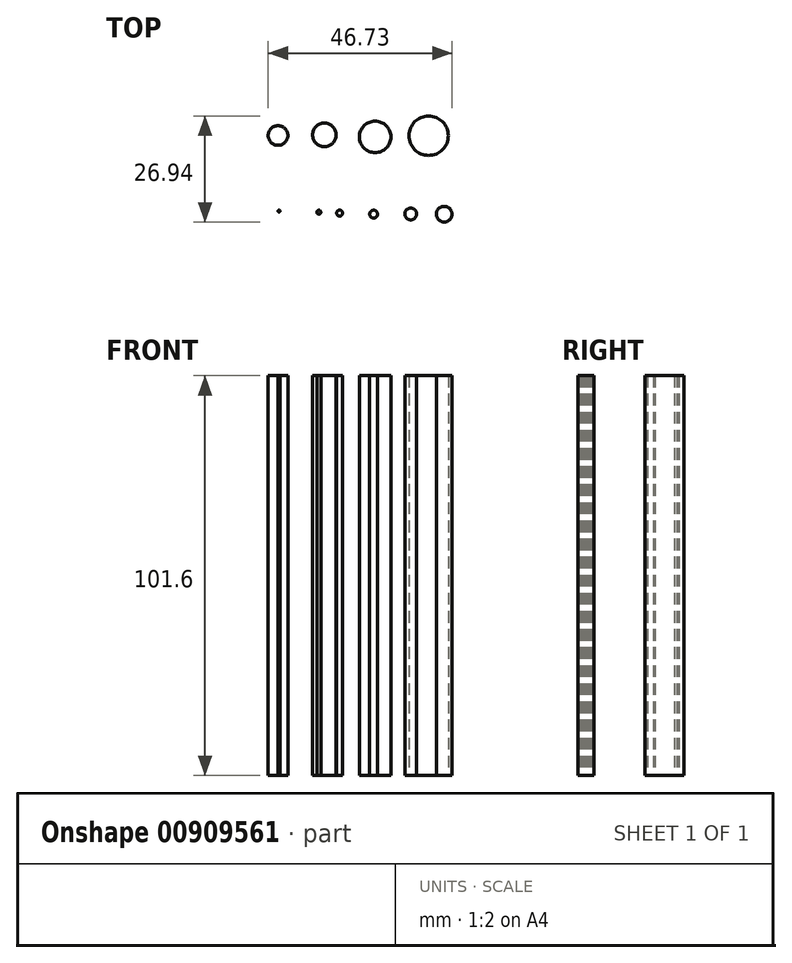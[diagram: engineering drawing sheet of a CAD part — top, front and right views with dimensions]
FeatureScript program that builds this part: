
annotation { "Feature Type Name" : "Feature", "Feature Type Description" : "" }
export const myFeature = defineFeature(function(context is Context, id is Id, definition is map)
    precondition{}
    {
        {
            var Q0;
            Q0=qCreatedBy(makeId("Top.planeOp"),FACE);
            var sketch = newSketch(context, id + "F0", { "sketchPlane" : qUnion([Q0])});
            skCircle(sketch, "E0", {"center": v(27, 14.36) * mm, "radius": 0.25 * mm});
            skCircle(sketch, "E1", {"center": v(37.12, 14.05) * mm, "radius": 0.5 * mm});
            skCircle(sketch, "E2", {"center": v(42.38, 13.83) * mm, "radius": 0.75 * mm});
            skCircle(sketch, "E3", {"center": v(51.02, 13.56) * mm, "radius": 1 * mm});
            skCircle(sketch, "E4", {"center": v(60.43, 13.61) * mm, "radius": 1.5 * mm});
            skCircle(sketch, "E5", {"center": v(68.95, 13.55) * mm, "radius": 2 * mm});
            skCircle(sketch, "E6", {"center": v(26.72, 33.55) * mm, "radius": 2.5 * mm});
            skCircle(sketch, "E7", {"center": v(38.5, 33.7) * mm, "radius": 3 * mm});
            skCircle(sketch, "E8", {"center": v(64.99, 33.49) * mm, "radius": 5 * mm});
            skCircle(sketch, "E9", {"center": v(51.4, 33.2) * mm, "radius": 4 * mm});
            skSolve(sketch);
        }
        {
            var Q0;
            Q0=qSketchRegion(id+"F0",true);
            extrude(context, id + "F1", {"entities" : qUnion([Q0]), "depth" : 101.6 * mm, "offsetDistance" : 25 * mm});
        }
    });
